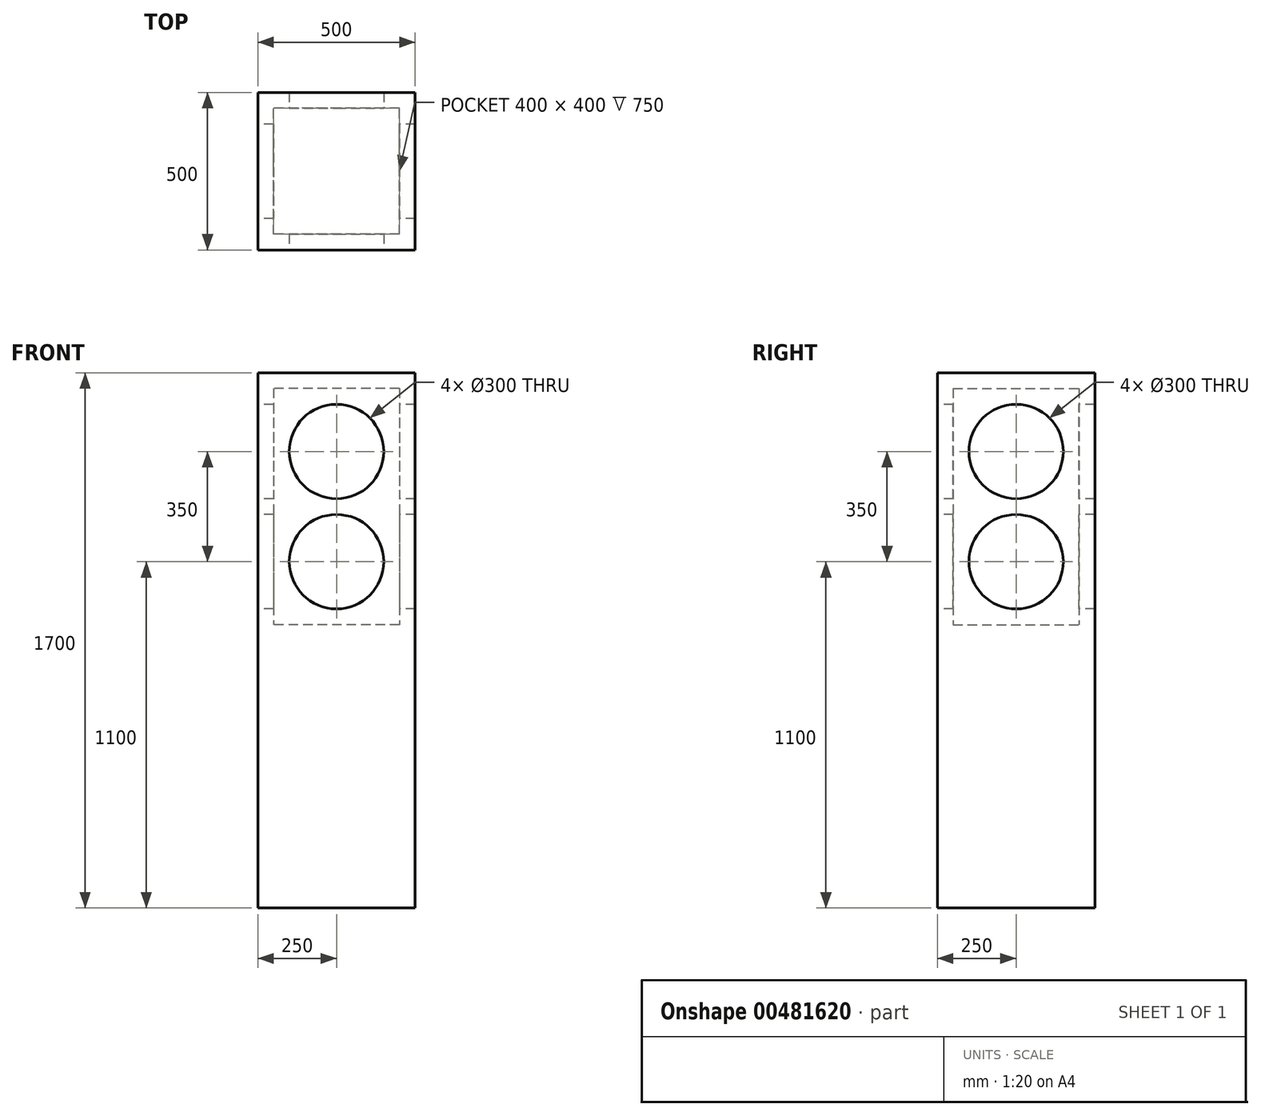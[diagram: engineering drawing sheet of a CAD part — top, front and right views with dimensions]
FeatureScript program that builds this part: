
annotation { "Feature Type Name" : "Feature", "Feature Type Description" : "" }
export const myFeature = defineFeature(function(context is Context, id is Id, definition is map)
    precondition{}
    {
        {
            var Q0;
            Q0=qCreatedBy(makeId("Top.planeOp"),FACE);
            var sketch = newSketch(context, id + "F0", { "sketchPlane" : qUnion([Q0])});
            skLineSegment(sketch, "E0.bottom", {"start": v(250, -250) * mm, "end": v(-250, -250) * mm});
            skLineSegment(sketch, "E0.top", {"start": v(250, 250) * mm, "end": v(-250, 250) * mm});
            skLineSegment(sketch, "E0.left", {"start": v(250, -250) * mm, "end": v(250, 250) * mm});
            skLineSegment(sketch, "E0.right", {"start": v(-250, -250) * mm, "end": v(-250, 250) * mm});
            skPoint(sketch, "E0.middle", {"position": v(0, 0) * mm});
            skSolve(sketch);
        }
        {
            var Q0;
            Q0 = qSketchRegion(id + "F0", true);
            extrude(context, id + "F1", {"entities" : qUnion([Q0]), "depth" : 850 * mm});
        }
        {
            var Q0;
            Q0=makeQuery(id+"F1.opExtrude","SWEPT_FACE",FACE,{"disambiguationData":[OSD([sQuery(id+"F0.wireOp",EDGE,"E0.bottom")])]});
            var sketch = newSketch(context, id + "F2", { "sketchPlane" : qUnion([Q0])});
            skCircle(sketch, "E1", {"center": v(0, 600) * mm, "radius": 150 * mm});
            skCircle(sketch, "E2", {"center": v(0, 250) * mm, "radius": 150 * mm});
            skSolve(sketch);
        }
        {
            var Q0;
            Q0 = qSketchRegion(id + "F2", true);
            extrude(context, id + "F3", {"entities" : qUnion([Q0]), "operationType" : NewBodyOperationType.REMOVE, "endBound" : BoundingType.THROUGH_ALL, "oppositeDirection" : true, "depth" : 25 * mm});
        }
        {
            var Q0;
            Q0=makeQuery(id+"F1.opExtrude","SWEPT_FACE",FACE,{"disambiguationData":[OSD([sQuery(id+"F0.wireOp",EDGE,"E0.right")])]});
            var sketch = newSketch(context, id + "F4", { "sketchPlane" : qUnion([Q0])});
            skCircle(sketch, "E3", {"center": v(0, 250) * mm, "radius": 150 * mm});
            skCircle(sketch, "E4", {"center": v(0, 600) * mm, "radius": 150 * mm});
            skSolve(sketch);
        }
        {
            var Q0;
            Q0 = qSketchRegion(id + "F4", true);
            extrude(context, id + "F5", {"entities" : qUnion([Q0]), "operationType" : NewBodyOperationType.REMOVE, "endBound" : BoundingType.THROUGH_ALL, "oppositeDirection" : true, "depth" : 25 * mm});
        }
        {
            var Q0;
            Q0=makeQuery(id+"F1.opExtrude","CAP_FACE",FACE,{"disambiguationData":[OSD([sQuery(id+"F0.wireOp",EDGE,"E0.bottom"),sQuery(id+"F0.wireOp",EDGE,"E0.top"),sQuery(id+"F0.wireOp",EDGE,"E0.left"),sQuery(id+"F0.wireOp",EDGE,"E0.right")])],"isStart":true});
            var sketch = newSketch(context, id + "F6", { "sketchPlane" : qUnion([Q0])});
            skLineSegment(sketch, "E5.0", {"start": v(200, 200) * mm, "end": v(-200, 200) * mm});
            skLineSegment(sketch, "E5.1", {"start": v(200, 200) * mm, "end": v(200, -200) * mm});
            skLineSegment(sketch, "E5.2", {"start": v(200, -200) * mm, "end": v(-200, -200) * mm});
            skLineSegment(sketch, "E5.3", {"start": v(-200, 200) * mm, "end": v(-200, -200) * mm});
            skSolve(sketch);
        }
        {
            var Q0;
            Q0 = qSketchRegion(id + "F6", true);
            extrude(context, id + "F7", {"entities" : qUnion([Q0]), "operationType" : NewBodyOperationType.REMOVE, "oppositeDirection" : true, "depth" : 800 * mm});
        }
        {
            var Q0;
            Q0 = qSketchRegion(id + "F0", true);
            extrude(context, id + "F8", {"entities" : qUnion([Q0]), "oppositeDirection" : true, "depth" : 850 * mm});
        }
        {
            var Q0;
            Q0 = qSketchRegion(id + "F6", true);
            extrude(context, id + "F9", {"entities" : qUnion([Q0]), "operationType" : NewBodyOperationType.ADD, "oppositeDirection" : true, "depth" : 50 * mm});
        }
    });
